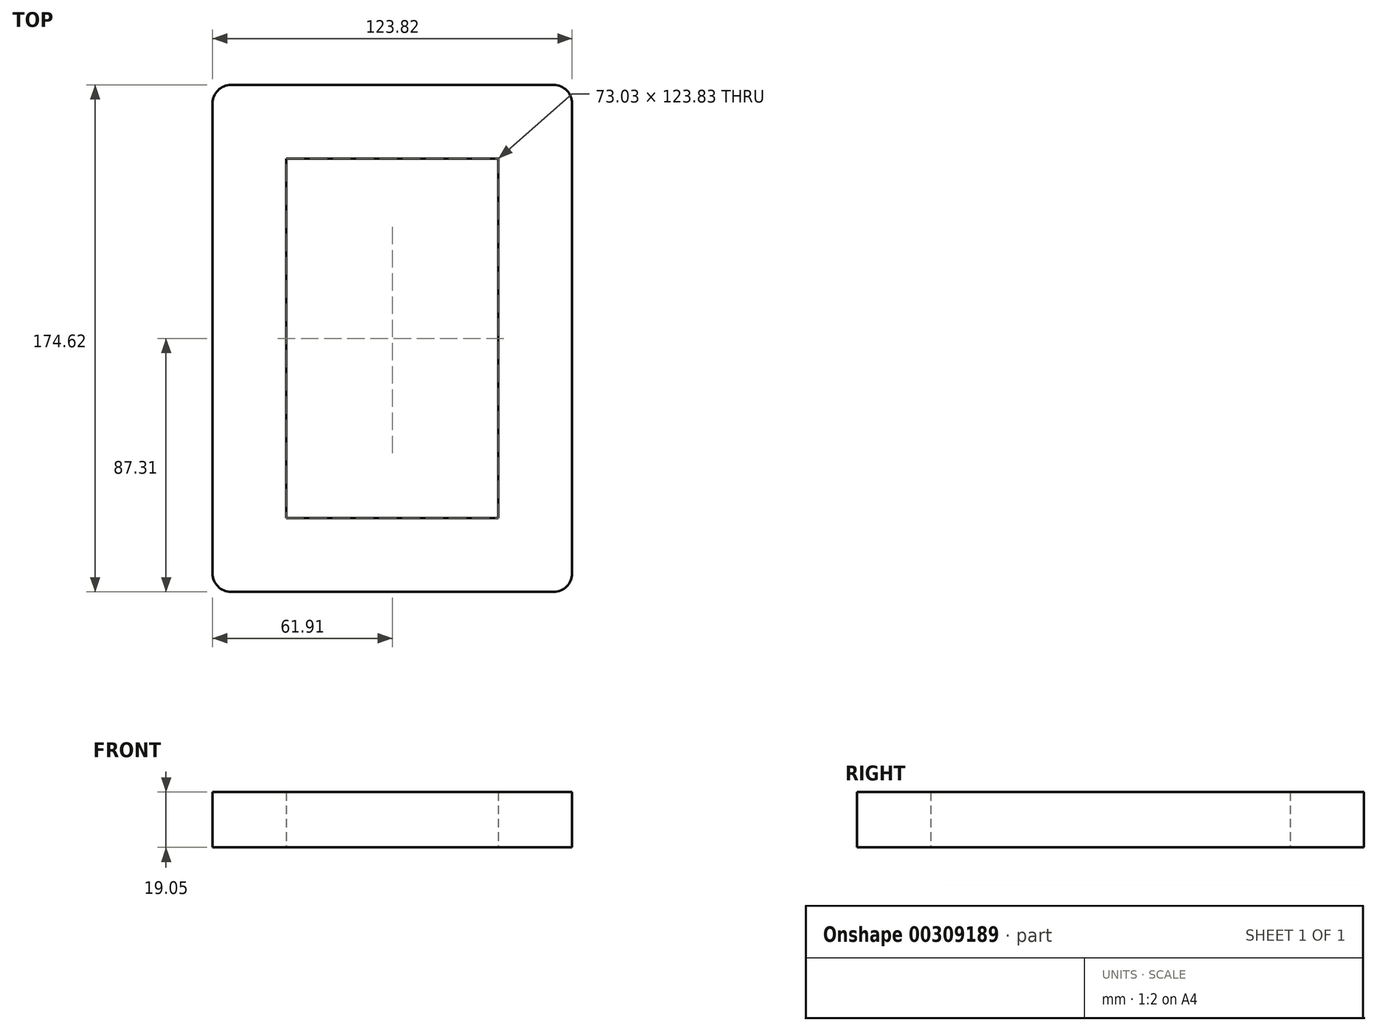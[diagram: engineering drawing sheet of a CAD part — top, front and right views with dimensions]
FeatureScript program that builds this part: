
annotation { "Feature Type Name" : "Feature", "Feature Type Description" : "" }
export const myFeature = defineFeature(function(context is Context, id is Id, definition is map)
    precondition{}
    {
        {
            var Q0;
            Q0=qCreatedBy(makeId("Top.planeOp"),FACE);
            var sketch = newSketch(context, id + "F0", { "sketchPlane" : qUnion([Q0])});
            skLineSegment(sketch, "E0.bottom", {"start": v(36.51, 61.91) * mm, "end": v(-36.51, 61.91) * mm});
            skLineSegment(sketch, "E0.top", {"start": v(36.51, -61.91) * mm, "end": v(-36.51, -61.91) * mm});
            skLineSegment(sketch, "E0.left", {"start": v(36.51, 61.91) * mm, "end": v(36.51, -61.91) * mm});
            skLineSegment(sketch, "E0.right", {"start": v(-36.51, 61.91) * mm, "end": v(-36.51, -61.91) * mm});
            skPoint(sketch, "E0.middle", {"position": v(0, 0) * mm});
            skLineSegment(sketch, "E1.0", {"start": v(55.56, 87.31) * mm, "end": v(-55.56, 87.31) * mm});
            skLineSegment(sketch, "E1.1", {"start": v(61.91, 80.96) * mm, "end": v(61.91, -80.96) * mm});
            skLineSegment(sketch, "E1.2", {"start": v(55.56, -87.31) * mm, "end": v(-55.56, -87.31) * mm});
            skLineSegment(sketch, "E1.3", {"start": v(-61.91, 80.96) * mm, "end": v(-61.91, -80.96) * mm});
            skPoint(sketch, "E2.visualSharp", {"position": v(-61.91, 87.31) * mm});
            skArc(sketch, "E2.filletArc", {"start": v(-55.56, 87.31) * mm, "mid": v(-60.05, 85.45) * mm, "end": v(-61.91, 80.96) * mm});
            skPoint(sketch, "E3.visualSharp", {"position": v(61.91, 87.31) * mm});
            skArc(sketch, "E3.filletArc", {"start": v(61.91, 80.96) * mm, "mid": v(60.05, 85.45) * mm, "end": v(55.56, 87.31) * mm});
            skPoint(sketch, "E4.visualSharp", {"position": v(61.91, -87.31) * mm});
            skArc(sketch, "E4.filletArc", {"start": v(55.56, -87.31) * mm, "mid": v(60.05, -85.45) * mm, "end": v(61.91, -80.96) * mm});
            skPoint(sketch, "E5.visualSharp", {"position": v(-61.91, -87.31) * mm});
            skArc(sketch, "E5.filletArc", {"start": v(-61.91, -80.96) * mm, "mid": v(-60.05, -85.45) * mm, "end": v(-55.56, -87.31) * mm});
            skSolve(sketch);
        }
        {
            var Q0;
            Q0=makeQuery(id+"F0.imprint","IMPRINT",FACE,{"disambiguationData":[TD([[makeQuery(id+"F0.imprint","IMPRINT",EDGE,{"derivedFrom":sQuery(id+"F0.wireOp",EDGE,"E0.bottom")}),-1.0]])]});
            extrude(context, id + "F1", {"entities" : qUnion([Q0]), "depth" : 19.05 * mm});
        }
    });
